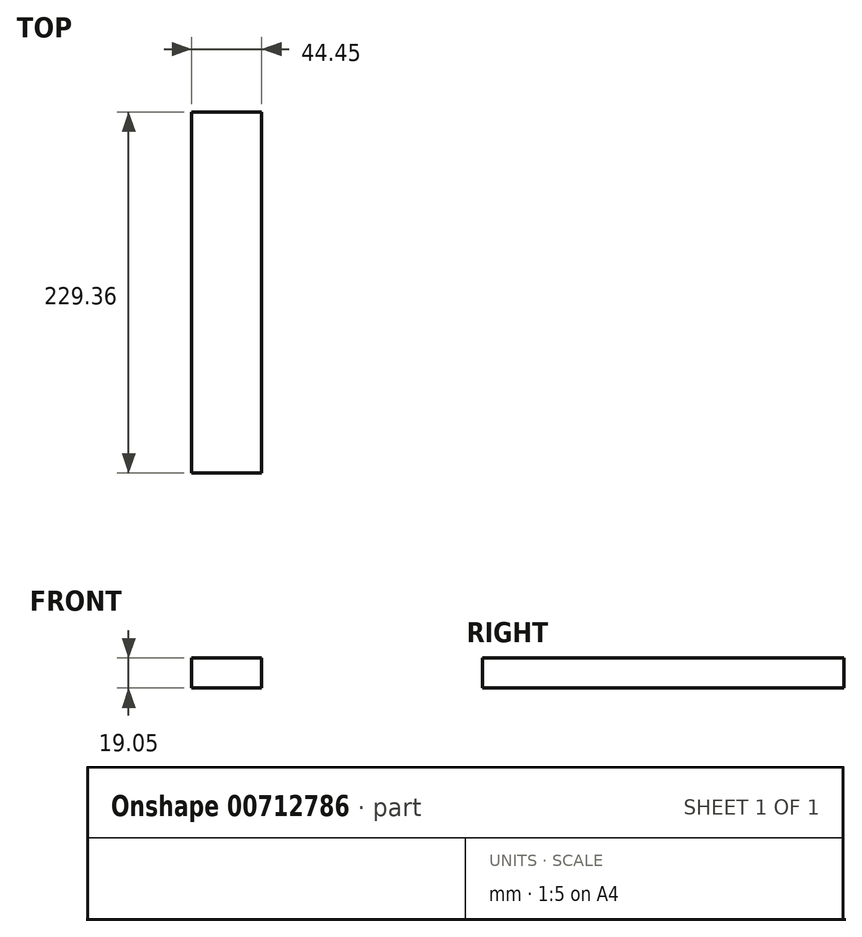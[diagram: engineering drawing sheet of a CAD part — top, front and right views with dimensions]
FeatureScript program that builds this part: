
annotation { "Feature Type Name" : "Feature", "Feature Type Description" : "" }
export const myFeature = defineFeature(function(context is Context, id is Id, definition is map)
    precondition{}
    {
        {
            var Q0;
            Q0=qCreatedBy(makeId("Front.planeOp"),FACE);
            var sketch = newSketch(context, id + "F0", { "sketchPlane" : qUnion([Q0])});
            skLineSegment(sketch, "E0.bottom", {"start": v(0, 0) * mm, "end": v(-44.45, 0) * mm});
            skLineSegment(sketch, "E0.top", {"start": v(0, 19.05) * mm, "end": v(-44.45, 19.05) * mm});
            skLineSegment(sketch, "E0.left", {"start": v(0, 0) * mm, "end": v(0, 19.05) * mm});
            skLineSegment(sketch, "E0.right", {"start": v(-44.45, 0) * mm, "end": v(-44.45, 19.05) * mm});
            skSolve(sketch);
        }
        {
            var Q0;
            Q0 = qSketchRegion(id + "F0", true);
            extrude(context, id + "F1", {"entities" : qUnion([Q0]), "depth" : 229.36 * mm, "offsetDistance" : 25.4 * mm});
        }
    });
